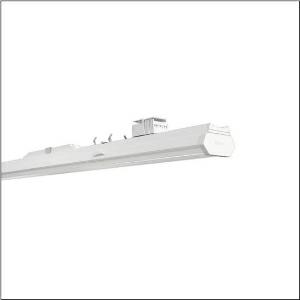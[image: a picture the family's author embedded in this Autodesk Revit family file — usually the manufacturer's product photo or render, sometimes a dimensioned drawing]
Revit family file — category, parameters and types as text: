
# Revit family: licross_r__11_protected_mo_51ts12vn455f_a2cc
name_source: partatom
category: Lighting Fixtures
units: mm (PartAtom-declared; Revit-internal decimal feet)

## family parameters
Cut with Voids When Loaded = No
Host = Face
Light Source = No
Part Type = Normal
Room Calculation Point = No
Round Connector Dimension = Use Diameter
Shared = No

## types (1)
- --- (1 x LED, 5510 lm, 35.8 W, 4000K)
    Apparent Load = 36 VA
    CIE Flux Codes = 54 82 95 97 100
    Color Rendering = 80
    Color Temperature = 4000K
    Default Elevation = 1800 mm
    Description = Licross® 11 Protected MOluminaire insert, length: 1.500mm, width: 90mm, height: 101mm, LED rated luminous flux: 5.510lm, light colour: 840, control gear: DALI 2, CLO, control gear: ECG DALI, with plug, 5-pole, with phase selection, mains connection: 220..240V, AC, 50/60Hz, halogen-free wiring, primary optical cover: cover, of PMMA, light emission: direct with ceiling illumination distribution, protection rating (complete): IP50, insulation class (complete): insulation class I (protective earthing), certification: CE, ENEC, VDE, UKCA, protection symbol: D if used in an environment with non-conductive dust loads with corresponding accessories, permissible ambient temperature for indoor applications: -25..+45°C, corresponds to IFS (International Featured Standards) requirements for safety and quality in the food industry, reducing of maximum allowable ambient temperature of 5°C with ceiling mounting, packaging unit: 1 piece
    Height = 92 mm
    Lamp = 1 x LED
    Lamp Light Flux = 5510 lm
    Lamp Power = 35.8 W
    Lamp count = 1
    Length = 1500 mm
    Luminous efficacy = 154 lm/W
    Manufacturer = Siteco
    ModVariant = No
    Model = 51TS12VN455F
    Mounting Place = Ceiling
    Mounting Type = Pendant
    Number of Poles = 1
    OnlyDefault = Yes
    Power Factor = 1
    Product Name = Licross® 11 Protected MO
    Product group = luminaire insert
    ProductGroupID = 902
    Protection Class = Protection class I
    Protection Degree = IP 50
    RLX_Detail_Level = 1
    RlxData = <blob elided: 24137 chars, md5=f2d3cd6c>
    Socket = socket
    Standby Power = 0 W
    System Light Flux = 5510 lm
    System Power = 36 W
    Type Comments = factory setting: luminous flux: 100 % | dim-lin: 254 | 235 mA
    Type Image = l_1256145.jpg
    URL = http://relux.com
    VarID = @adj_129407
    Voltage = 0 V
    Weight = 0.00 kg
    Width = 88 mm

## geometry (parser evidence)
native form markers: Blend x4, Sweep x12
no freeform markers — native parametric forms only
